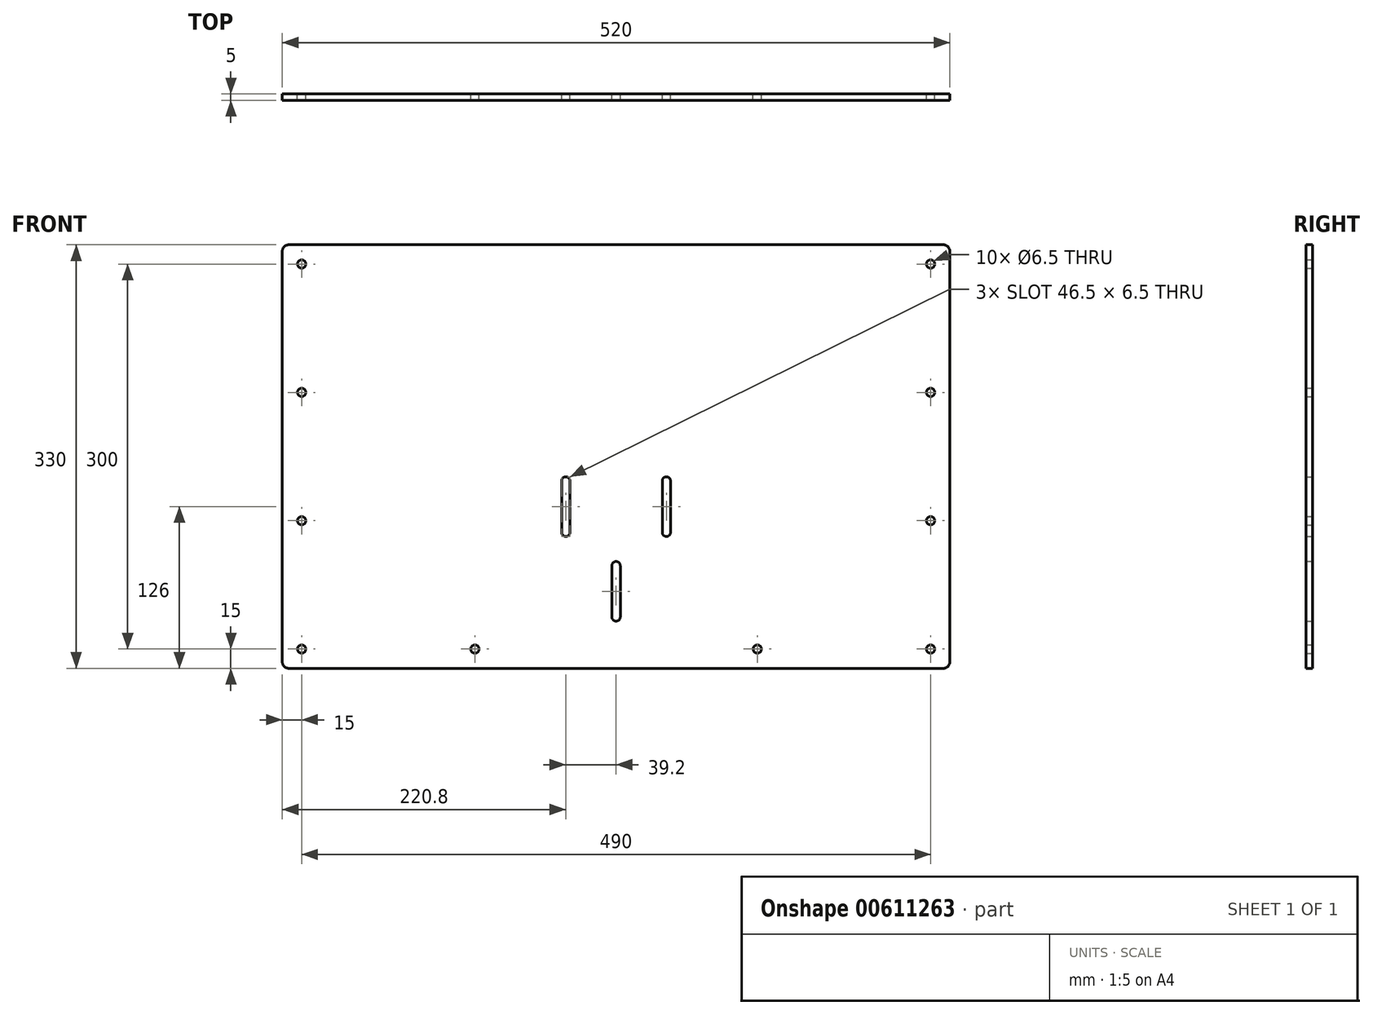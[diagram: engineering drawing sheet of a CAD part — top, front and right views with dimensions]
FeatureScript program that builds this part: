
annotation { "Feature Type Name" : "Feature", "Feature Type Description" : "" }
export const myFeature = defineFeature(function(context is Context, id is Id, definition is map)
    precondition{}
    {
        {
            var Q0;
            Q0=qCreatedBy(makeId("Front.planeOp"),FACE);
            var sketch = newSketch(context, id + "F0", { "sketchPlane" : qUnion([Q0])});
            skLineSegment(sketch, "E0.bottom", {"start": v(0, 0) * mm, "end": v(520, 0) * mm});
            skLineSegment(sketch, "E0.top", {"start": v(0, 330) * mm, "end": v(520, 330) * mm});
            skLineSegment(sketch, "E0.left", {"start": v(0, 0) * mm, "end": v(0, 330) * mm});
            skLineSegment(sketch, "E0.right", {"start": v(520, 0) * mm, "end": v(520, 330) * mm});
            skCircle(sketch, "E1", {"center": v(15, 15) * mm, "radius": 3.25 * mm});
            skCircle(sketch, "E2", {"center": v(15, 115) * mm, "radius": 3.25 * mm});
            skCircle(sketch, "E3", {"center": v(15, 215) * mm, "radius": 3.25 * mm});
            skCircle(sketch, "E4", {"center": v(15, 315) * mm, "radius": 3.25 * mm});
            skCircle(sketch, "E5", {"center": v(150, 15) * mm, "radius": 3.25 * mm});
            skCircle(sketch, "E6", {"center": v(370, 15) * mm, "radius": 3.25 * mm});
            skCircle(sketch, "E7", {"center": v(505, 15) * mm, "radius": 3.25 * mm});
            skCircle(sketch, "E8", {"center": v(505, 115) * mm, "radius": 3.25 * mm});
            skCircle(sketch, "E9", {"center": v(505, 215) * mm, "radius": 3.25 * mm});
            skCircle(sketch, "E10", {"center": v(505, 315) * mm, "radius": 3.25 * mm});
            skLineSegment(sketch, "E11", {"start": v(260, 330) * mm, "end": v(260, 0) * mm, "construction": true});
            skCircle(sketch, "E12", {"center": v(260, 60) * mm, "radius": 3.25 * mm, "construction": true});
            skLineSegment(sketch, "E13", {"start": v(299.2, 126) * mm, "end": v(260, 126) * mm, "construction": true});
            skLineSegment(sketch, "E14", {"start": v(260, 126) * mm, "end": v(220.8, 126) * mm, "construction": true});
            skCircle(sketch, "E15", {"center": v(299.2, 126) * mm, "radius": 3.25 * mm, "construction": true});
            skCircle(sketch, "E16", {"center": v(220.8, 126) * mm, "radius": 3.25 * mm, "construction": true});
            skLineSegment(sketch, "E17", {"start": v(220.8, 146) * mm, "end": v(220.8, 106) * mm, "construction": true});
            skArc(sketch, "E18.0.startCap", {"start": v(217.55, 146) * mm, "mid": v(220.8, 149.25) * mm, "end": v(224.05, 146) * mm});
            skArc(sketch, "E18.0.endCap", {"start": v(224.05, 106) * mm, "mid": v(220.8, 102.75) * mm, "end": v(217.55, 106) * mm});
            skLineSegment(sketch, "E18.0.left", {"start": v(224.05, 146) * mm, "end": v(224.05, 106) * mm});
            skLineSegment(sketch, "E18.0.right", {"start": v(217.55, 146) * mm, "end": v(217.55, 106) * mm});
            skLineSegment(sketch, "E19", {"start": v(299.2, 146) * mm, "end": v(299.2, 106) * mm, "construction": true});
            skArc(sketch, "E20.0.startCap", {"start": v(295.95, 146) * mm, "mid": v(299.2, 149.25) * mm, "end": v(302.45, 146) * mm});
            skArc(sketch, "E20.0.endCap", {"start": v(302.45, 106) * mm, "mid": v(299.2, 102.75) * mm, "end": v(295.95, 106) * mm});
            skLineSegment(sketch, "E20.0.left", {"start": v(302.45, 146) * mm, "end": v(302.45, 106) * mm});
            skLineSegment(sketch, "E20.0.right", {"start": v(295.95, 146) * mm, "end": v(295.95, 106) * mm});
            skLineSegment(sketch, "E21", {"start": v(260, 80) * mm, "end": v(260, 40) * mm});
            skArc(sketch, "E22.0.startCap", {"start": v(256.75, 80) * mm, "mid": v(260, 83.25) * mm, "end": v(263.25, 80) * mm});
            skArc(sketch, "E22.0.endCap", {"start": v(263.25, 40) * mm, "mid": v(260, 36.75) * mm, "end": v(256.75, 40) * mm});
            skLineSegment(sketch, "E22.0.left", {"start": v(263.25, 80) * mm, "end": v(263.25, 40) * mm});
            skLineSegment(sketch, "E22.0.right", {"start": v(256.75, 80) * mm, "end": v(256.75, 40) * mm});
            skSolve(sketch);
        }
        {
            var Q0;
            Q0=makeQuery(id+"F0.imprint","IMPRINT",FACE,{"disambiguationData":[TD([[makeQuery(id+"F0.imprint","IMPRINT",EDGE,{"derivedFrom":sQuery(id+"F0.wireOp",EDGE,"E0.bottom")}),1.0]])]});
            extrude(context, id + "F1", {"entities" : qUnion([Q0]), "depth" : 5 * mm, "offsetDistance" : 25 * mm});
        }
        {
            var Q0;
            Q0=makeQuery(id+"F1.opExtrude","SWEPT_EDGE",EDGE,{"disambiguationData":[OSD([sQuery(id+"F0.wireOp",EDGE,"E0.top"),sQuery(id+"F0.wireOp",EDGE,"E0.right")])]});
            var Q1;
            Q1=makeQuery(id+"F1.opExtrude","SWEPT_EDGE",EDGE,{"disambiguationData":[OSD([sQuery(id+"F0.wireOp",EDGE,"E0.bottom"),sQuery(id+"F0.wireOp",EDGE,"E0.right")])]});
            var Q2;
            Q2=makeQuery(id+"F1.opExtrude","SWEPT_EDGE",EDGE,{"disambiguationData":[OSD([sQuery(id+"F0.wireOp",EDGE,"E0.bottom"),sQuery(id+"F0.wireOp",EDGE,"E0.left")])]});
            var Q3;
            Q3=makeQuery(id+"F1.opExtrude","SWEPT_EDGE",EDGE,{"disambiguationData":[OSD([sQuery(id+"F0.wireOp",EDGE,"E0.top"),sQuery(id+"F0.wireOp",EDGE,"E0.left")])]});
            fillet(context, id + "F2", {"entities" : qUnion([Q0, Q1, Q2, Q3]), "radius" : 5 * mm, "tangentPropagation" : true, "allowEdgeOverflow" : false});
        }
    });
